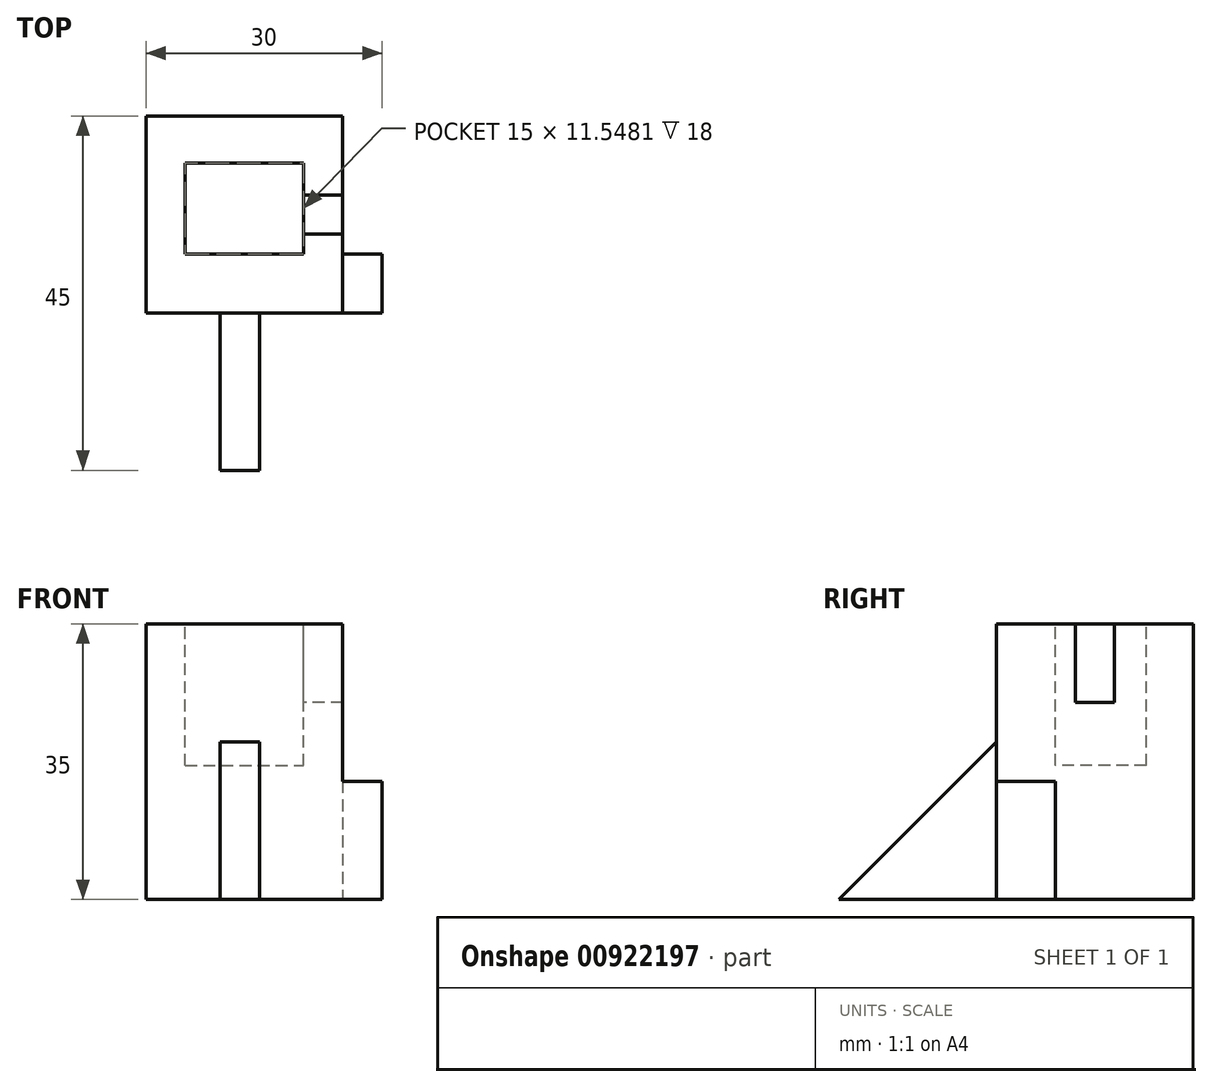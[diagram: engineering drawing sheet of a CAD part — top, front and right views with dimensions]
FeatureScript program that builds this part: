
annotation { "Feature Type Name" : "Feature", "Feature Type Description" : "" }
export const myFeature = defineFeature(function(context is Context, id is Id, definition is map)
    precondition{}
    {
        {
            var Q0;
            Q0=qCreatedBy(makeId("Top.planeOp"),FACE);
            var sketch = newSketch(context, id + "F0", { "sketchPlane" : qUnion([Q0])});
            skLineSegment(sketch, "E0", {"start": v(-13.32, 8.98) * mm, "end": v(11.68, 8.98) * mm});
            skLineSegment(sketch, "E1", {"start": v(11.68, 8.98) * mm, "end": v(11.68, -16.02) * mm});
            skLineSegment(sketch, "E2", {"start": v(11.68, -16.02) * mm, "end": v(-13.32, -16.02) * mm});
            skLineSegment(sketch, "E3", {"start": v(-13.32, -16.02) * mm, "end": v(-13.32, 8.98) * mm});
            skSolve(sketch);
        }
        {
            var Q0;
            Q0 = qSketchRegion(id + "F0", true);
            extrude(context, id + "F1", {"entities" : qUnion([Q0]), "depth" : 35 * mm, "offsetDistance" : 25 * mm});
        }
        {
            var Q0;
            Q0=makeQuery(id+"F1.opExtrude","SWEPT_FACE",FACE,{"disambiguationData":[OSD([sQuery(id+"F0.wireOp",EDGE,"E1")])]});
            var sketch = newSketch(context, id + "F2", { "sketchPlane" : qUnion([Q0])});
            skLineSegment(sketch, "E4", {"start": v(-16.02, 0) * mm, "end": v(-16.02, 15) * mm});
            skLineSegment(sketch, "E5", {"start": v(-16.02, 15) * mm, "end": v(-8.52, 15) * mm});
            skLineSegment(sketch, "E6", {"start": v(-8.52, 15) * mm, "end": v(-8.52, 0) * mm});
            skSolve(sketch);
        }
        {
            var Q0;
            Q0 = qSketchRegion(id + "F2", true);
            var Q1;
            {var subQ0=sQuery(id+"F2.wireOp",EDGE,"E4");Q1=makeQuery(id+"F2.imprint","IMPRINT",FACE,{"disambiguationData":[TD([[makeQuery(id+"F2.imprint","IMPRINT",EDGE,{"derivedFrom":subQ0}),1.0]])]});}
            extrude(context, id + "F3", {"entities" : qUnion([Q0, Q1]), "operationType" : NewBodyOperationType.ADD, "depth" : 5 * mm, "offsetDistance" : 25 * mm});
        }
        {
            var Q0;
            Q0=makeQuery(id+"F1.opExtrude","CAP_FACE",FACE,{"disambiguationData":[OSD([sQuery(id+"F0.wireOp",EDGE,"E0"),sQuery(id+"F0.wireOp",EDGE,"E1"),sQuery(id+"F0.wireOp",EDGE,"E2"),sQuery(id+"F0.wireOp",EDGE,"E3")])],"isStart":false});
            var sketch = newSketch(context, id + "F4", { "sketchPlane" : qUnion([Q0])});
            skLineSegment(sketch, "E7", {"start": v(11.68, -1.02) * mm, "end": v(6.68, -1.02) * mm});
            skLineSegment(sketch, "E8", {"start": v(6.68, -1.02) * mm, "end": v(6.68, -6.02) * mm});
            skLineSegment(sketch, "E9", {"start": v(6.68, -6.02) * mm, "end": v(11.68, -6.02) * mm});
            skSolve(sketch);
        }
        {
            var Q0;
            Q0 = qSketchRegion(id + "F4", true);
            var Q1;
            {var subQ0=sQuery(id+"F4.wireOp",EDGE,"E7");Q1=makeQuery(id+"F4.imprint","IMPRINT",FACE,{"disambiguationData":[TD([[makeQuery(id+"F4.imprint","IMPRINT",EDGE,{"derivedFrom":subQ0}),1.0]])]});}
            extrude(context, id + "F5", {"entities" : qUnion([Q0, Q1]), "operationType" : NewBodyOperationType.REMOVE, "oppositeDirection" : true, "depth" : 10 * mm, "offsetDistance" : 25 * mm});
        }
        {
            var Q0;
            Q0=makeQuery(id+"F1.opExtrude","CAP_FACE",FACE,{"disambiguationData":[OSD([sQuery(id+"F0.wireOp",EDGE,"E0"),sQuery(id+"F0.wireOp",EDGE,"E1"),sQuery(id+"F0.wireOp",EDGE,"E2"),sQuery(id+"F0.wireOp",EDGE,"E3")])],"isStart":false});
            var sketch = newSketch(context, id + "F6", { "sketchPlane" : qUnion([Q0])});
            skLineSegment(sketch, "E10", {"start": v(-8.32, 3.03) * mm, "end": v(6.68, 3.03) * mm});
            skLineSegment(sketch, "E11", {"start": v(6.68, 3.03) * mm, "end": v(6.68, -1.02) * mm});
            skLineSegment(sketch, "E12", {"start": v(6.68, -8.52) * mm, "end": v(-8.32, -8.52) * mm});
            skLineSegment(sketch, "E13", {"start": v(-8.32, -8.52) * mm, "end": v(-8.32, 3.03) * mm});
            skLineSegment(sketch, "E14", {"start": v(6.68, -6.02) * mm, "end": v(6.68, -8.52) * mm});
            skSolve(sketch);
        }
        {
            var Q0;
            Q0 = qSketchRegion(id + "F6", true);
            var Q1;
            Q1=makeQuery(id+"F6.imprint","IMPRINT",FACE,{"disambiguationData":[TD([[makeQuery(id+"F6.imprint","IMPRINT",EDGE,{"derivedFrom":sQuery(id+"F6.wireOp",EDGE,"E10")}),-1.0]])]});
            extrude(context, id + "F7", {"entities" : qUnion([Q0, Q1]), "operationType" : NewBodyOperationType.REMOVE, "oppositeDirection" : true, "depth" : 18 * mm, "offsetDistance" : 25 * mm});
        }
        {
            var Q0;
            Q0=makeQuery(id+"F3.boolean.opBoolean","MERGE",FACE,{"derivedFrom":[makeQuery(id+"F1.opExtrude","SWEPT_FACE",FACE,{"disambiguationData":[OSD([sQuery(id+"F0.wireOp",EDGE,"E2")])]}),makeQuery(id+"F3.opExtrude","SWEPT_FACE",FACE,{"disambiguationData":[OSD([sQuery(id+"F2.wireOp",EDGE,"E4")])]})]});
            var sketch = newSketch(context, id + "F8", { "sketchPlane" : qUnion([Q0])});
            skLineSegment(sketch, "E15", {"start": v(-3.9, 20) * mm, "end": v(1.1, 20) * mm});
            skLineSegment(sketch, "E16", {"start": v(1.1, 20) * mm, "end": v(1.1, 0) * mm});
            skLineSegment(sketch, "E17", {"start": v(1.1, 0) * mm, "end": v(-3.9, 0) * mm});
            skLineSegment(sketch, "E18", {"start": v(-3.9, 0) * mm, "end": v(-3.9, 20) * mm});
            skSolve(sketch);
        }
        {
            var Q0;
            Q0=makeQuery(id+"F8.imprint","IMPRINT",FACE,{"disambiguationData":[TD([[makeQuery(id+"F8.imprint","IMPRINT",EDGE,{"derivedFrom":sQuery(id+"F8.wireOp",EDGE,"E15")}),-1.0]])]});
            extrude(context, id + "F9", {"entities" : qUnion([Q0]), "operationType" : NewBodyOperationType.ADD, "depth" : 20 * mm, "offsetDistance" : 25 * mm});
        }
        {
            var Q0;
            Q0=makeQuery(id+"F9.opExtrude","SWEPT_FACE",FACE,{"disambiguationData":[OSD([sQuery(id+"F8.wireOp",EDGE,"E18")])]});
            var sketch = newSketch(context, id + "F10", { "sketchPlane" : qUnion([Q0])});
            skLineSegment(sketch, "E19", {"start": v(16.02, 20) * mm, "end": v(36.02, 20) * mm});
            skLineSegment(sketch, "E20", {"start": v(36.02, 20) * mm, "end": v(36.02, 0) * mm});
            skLineSegment(sketch, "E21", {"start": v(36.02, 0) * mm, "end": v(16.02, 20) * mm});
            skSolve(sketch);
        }
        {
            var Q0;
            Q0=makeQuery(id+"F10.imprint","IMPRINT",FACE,{"disambiguationData":[TD([[makeQuery(id+"F10.imprint","IMPRINT",EDGE,{"derivedFrom":sQuery(id+"F10.wireOp",EDGE,"E19")}),1.0]])]});
            extrude(context, id + "F11", {"entities" : qUnion([Q0]), "operationType" : NewBodyOperationType.REMOVE, "oppositeDirection" : true, "depth" : 29.5 * mm, "offsetDistance" : 25 * mm});
        }
    });
